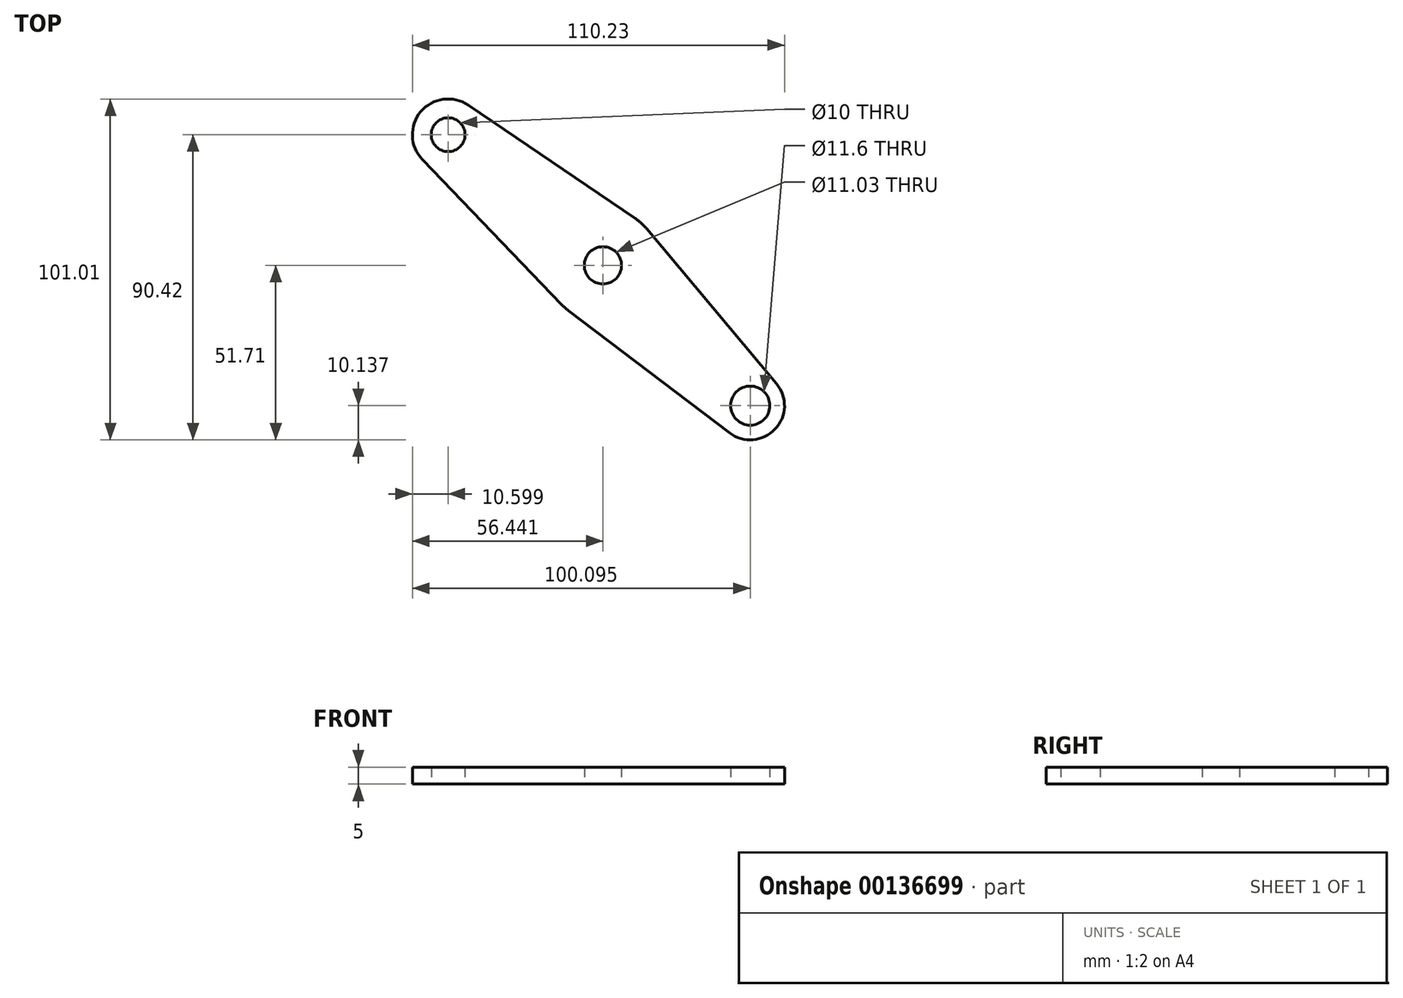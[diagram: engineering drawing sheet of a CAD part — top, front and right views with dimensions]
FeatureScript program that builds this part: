
annotation { "Feature Type Name" : "Feature", "Feature Type Description" : "" }
export const myFeature = defineFeature(function(context is Context, id is Id, definition is map)
    precondition{}
    {
        {
            var Q0;
            Q0=qCreatedBy(makeId("Top.planeOp"),FACE);
            var sketch = newSketch(context, id + "F0", { "sketchPlane" : qUnion([Q0])});
            skCircle(sketch, "E0", {"center": v(-43.94, 50.4) * mm, "radius": 5 * mm});
            skCircle(sketch, "E1", {"center": v(-43.94, 50.4) * mm, "radius": 10.6 * mm});
            skCircle(sketch, "E2", {"center": v(1.9, 11.69) * mm, "radius": 16.89 * mm});
            skCircle(sketch, "E3", {"center": v(1.9, 11.69) * mm, "radius": 5.52 * mm});
            skCircle(sketch, "E4", {"center": v(45.55, -29.88) * mm, "radius": 5.8 * mm});
            skCircle(sketch, "E5", {"center": v(45.55, -29.88) * mm, "radius": 10.14 * mm});
            skLineSegment(sketch, "E6", {"start": v(-38, 59.17) * mm, "end": v(11.38, 25.67) * mm});
            skLineSegment(sketch, "E7", {"start": v(-51.59, 43.07) * mm, "end": v(-10.29, 0) * mm});
            skLineSegment(sketch, "E8", {"start": v(14.85, 22.54) * mm, "end": v(53.32, -23.37) * mm});
            skLineSegment(sketch, "E9", {"start": v(39.43, -37.96) * mm, "end": v(-8.3, -1.77) * mm});
            skLineSegment(sketch, "E10", {"start": v(-43.94, 50.4) * mm, "end": v(1.9, 11.69) * mm});
            skSolve(sketch);
        }
        {
            var Q0;
            Q0 = qSketchRegion(id + "F0", true);
            extrude(context, id + "F1", {"entities" : qUnion([Q0]), "depth" : 5 * mm});
        }
    });
